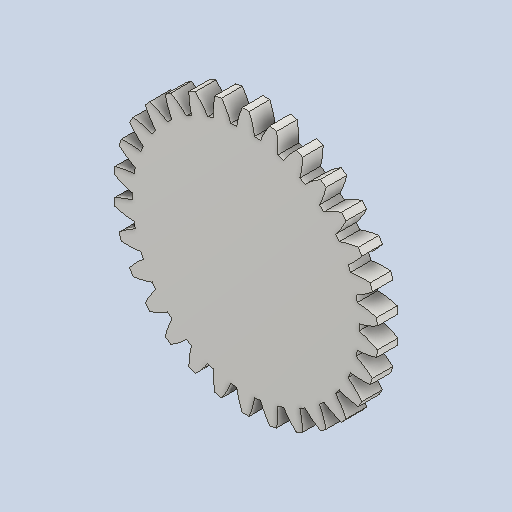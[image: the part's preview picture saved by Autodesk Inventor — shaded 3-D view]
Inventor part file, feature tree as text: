
AUTODESK INVENTOR PART (.ipt)
format: ipt  version: 2023 (Build 270158000, 158)  size: 259,072 bytes
history: native  units: mm (DEFAULTED — no unit token found)
features: plane x3, other x3, sketch x2, extrude x1
ambient origin geometry x8: Origin, YZ Plane, XZ Plane, XY Plane, X Axis, Y Axis, Z Axis, Center Point
bodies: Solid1 (feature_tree)
feature tree (9):
  extrude  "Extrusion1"  Depth=5.0mm TaperAngle=0.0deg
  plane  "Work Plane2"
  plane  "Work Plane8"
  plane  "Work Plane9"
  other  "Spur Gear"
  sketch  "Sketch1"  dims[d0=64.0mm d1=5.0mm d2=0.0mm]
  sketch  "Sketch2"  dims[d3=60.0mm d4=10.0mm d5=0.0mm d16=40.0mm d17=0.0mm d34=1.047198mm d39=0.0mm d41=0.0mm d43=40.0mm d46=40.0mm d47=0.0mm d48=0.0mm]
  other  "Srf1"
  other  "Pitch Diameter"
